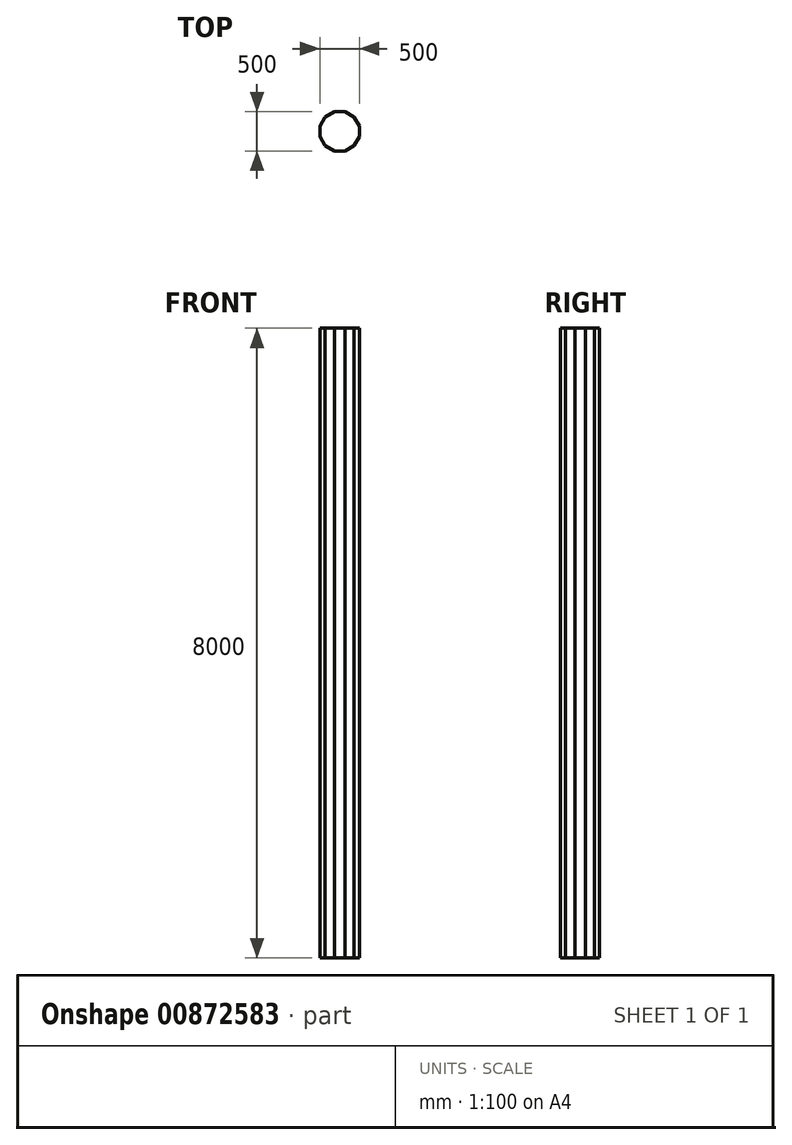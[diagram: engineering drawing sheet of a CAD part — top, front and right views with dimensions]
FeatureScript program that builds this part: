
annotation { "Feature Type Name" : "Feature", "Feature Type Description" : "" }
export const myFeature = defineFeature(function(context is Context, id is Id, definition is map)
    precondition{}
    {
        {
            var Q0;
            Q0=qCreatedBy(makeId("Top.planeOp"),FACE);
            var sketch = newSketch(context, id + "F0", { "sketchPlane" : qUnion([Q0])});
            skCircle(sketch, "E0.cCircle", {"center": v(0, 0) * mm, "radius": 250 * mm, "construction": true});
            skLineSegment(sketch, "E0.0", {"start": v(66.99, -250) * mm, "end": v(-66.99, -250) * mm});
            skLineSegment(sketch, "E0.1", {"start": v(-66.99, -250) * mm, "end": v(-183.01, -183.01) * mm});
            skLineSegment(sketch, "E0.2", {"start": v(-183.01, -183.01) * mm, "end": v(-250, -66.99) * mm});
            skLineSegment(sketch, "E0.3", {"start": v(-250, -66.99) * mm, "end": v(-250, 66.99) * mm});
            skLineSegment(sketch, "E0.4", {"start": v(-250, 66.99) * mm, "end": v(-183.01, 183.01) * mm});
            skLineSegment(sketch, "E0.5", {"start": v(-183.01, 183.01) * mm, "end": v(-66.99, 250) * mm});
            skLineSegment(sketch, "E0.6", {"start": v(-66.99, 250) * mm, "end": v(66.99, 250) * mm});
            skLineSegment(sketch, "E0.7", {"start": v(66.99, 250) * mm, "end": v(183.01, 183.01) * mm});
            skLineSegment(sketch, "E0.8", {"start": v(183.01, 183.01) * mm, "end": v(250, 66.99) * mm});
            skLineSegment(sketch, "E0.9", {"start": v(250, 66.99) * mm, "end": v(250, -66.99) * mm});
            skLineSegment(sketch, "E0.10", {"start": v(250, -66.99) * mm, "end": v(183.01, -183.01) * mm});
            skLineSegment(sketch, "E0.11", {"start": v(183.01, -183.01) * mm, "end": v(66.99, -250) * mm});
            skPoint(sketch, "E0.0.midPoint", {"position": v(0, -250) * mm});
            skSolve(sketch);
        }
        {
            var Q0;
            Q0=makeQuery(id+"F0.imprint","IMPRINT",FACE,{"disambiguationData":[TD([[makeQuery(id+"F0.imprint","IMPRINT",EDGE,{"derivedFrom":sQuery(id+"F0.wireOp",EDGE,"E0.0")}),-1.0]])]});
            extrude(context, id + "F1", {"entities" : qUnion([Q0]), "depth" : 8000 * mm, "offsetDistance" : 25 * mm});
        }
    });
